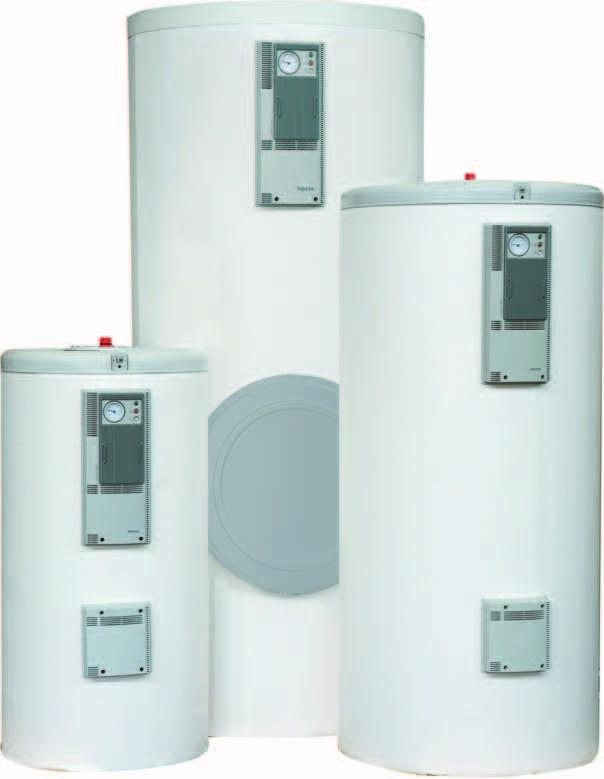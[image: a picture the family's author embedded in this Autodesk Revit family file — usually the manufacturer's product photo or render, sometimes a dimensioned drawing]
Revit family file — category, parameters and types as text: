
# Revit family: CV-200-HL_CC01790
name_source: partatom
category: Aparatos eléctricos
revit_build: Autodesk Revit 2016 (Build: 20150220_1215(x64)
units: mm (PartAtom-declared; Revit-internal decimal feet)

## family parameters
Compartido = No
Corte con vacíos al cargar = No
Cota de conector redondo = Diámetro de uso
Mantener orientación de anotación = No
Número OmniClass = 23.80.00.00
Punto de cálculo de habitación = No
Se basa en plano de trabajo = No
Siempre vertical = Sí
Tipo de pieza = Caja de conexiones
Título OmniClass = Electric Power and Lighting

## types (1)
- CV-200-HL
    Capacidad A.C.S. = 200 l
    Clase eficiencia energética = B
    Costo = 0 $
    Código de montaje = CC01790
    Descripción = DEPOSITOS DE ACERO VITRIFICADO
    Dimensiones = 620 x 1205 mm
    Fabricante = SALVADOR ESCODA
    Imagen de tipo = depositos_acero_vitrificado.jpg
    Modelo = CV-200-HL
    Peso vacío (aprox.) = 100 Kg
    Presión máx. circuito calentamiento = 2,5 (25) MPa (bar)
    Presión máx. depósito = 0,8 (8) MPa (bar)
    Pérdidas estáticas = 56W
    Superfície intercambio circuito calentamiento = 2,4 m2
    Temperatura máx. circuito calentamiento = 200 ºC
    Temperatura máx. depósito = 90 ºC
    URL = www.salvadorescoda.com
    Volúmen = 197 l
